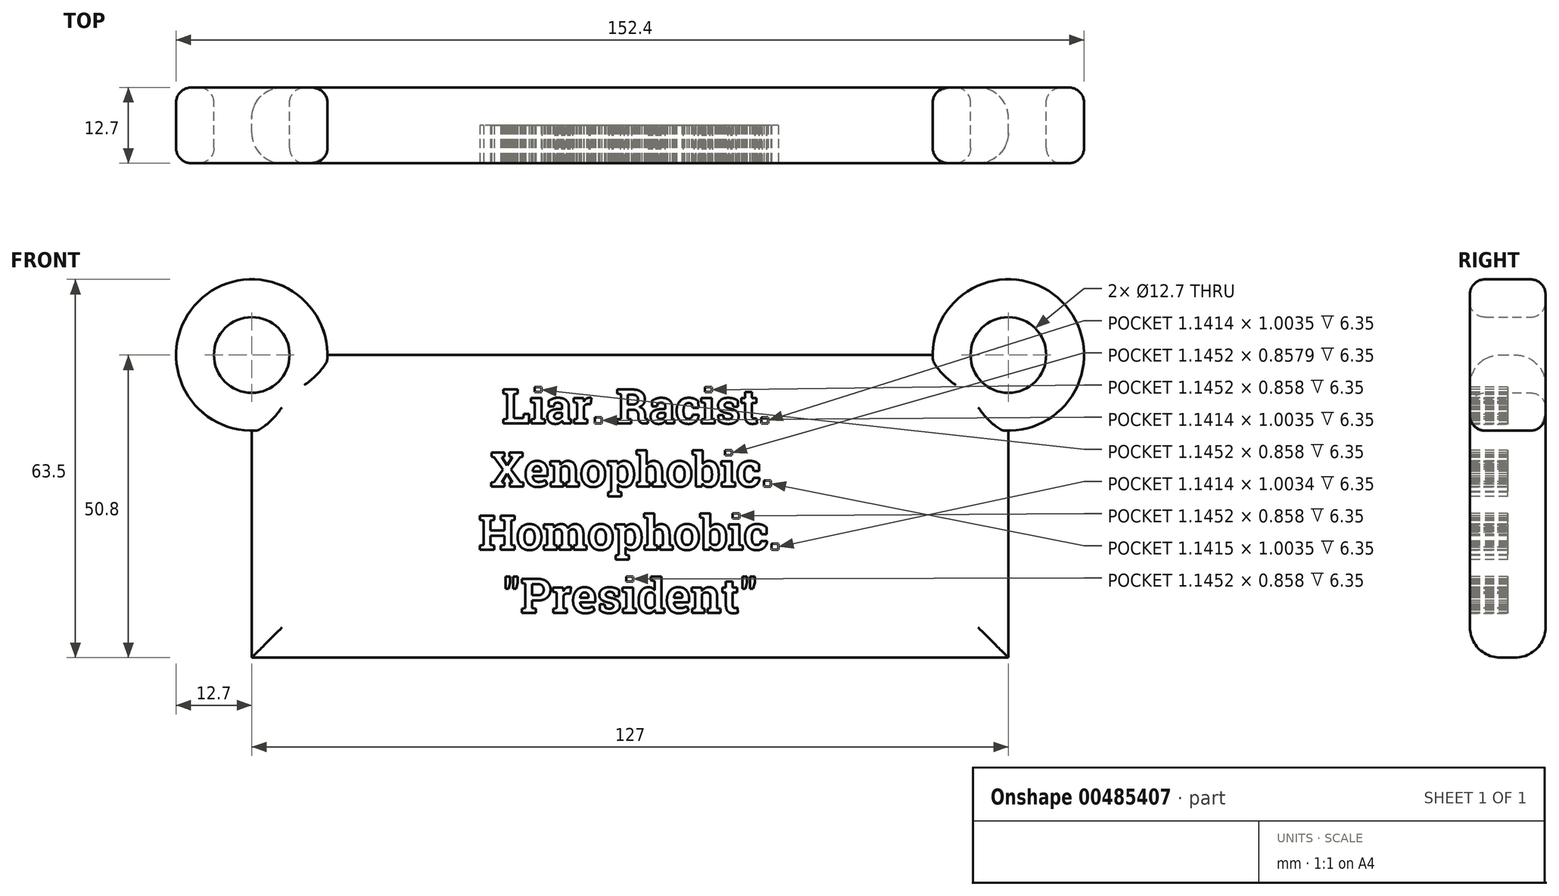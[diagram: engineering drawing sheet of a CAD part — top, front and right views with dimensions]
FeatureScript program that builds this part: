
annotation { "Feature Type Name" : "Feature", "Feature Type Description" : "" }
export const myFeature = defineFeature(function(context is Context, id is Id, definition is map)
    precondition{}
    {
        {
            var Q0;
            Q0=qCreatedBy(makeId("Front.planeOp"),FACE);
            var sketch = newSketch(context, id + "F0", { "sketchPlane" : qUnion([Q0])});
            skLineSegment(sketch, "E0.bottom", {"start": v(-127, 50.8) * mm, "end": v(0, 50.8) * mm});
            skLineSegment(sketch, "E0.top", {"start": v(-127, 0) * mm, "end": v(0, 0) * mm});
            skLineSegment(sketch, "E0.left", {"start": v(-127, 50.8) * mm, "end": v(-127, 0) * mm});
            skLineSegment(sketch, "E0.right", {"start": v(0, 50.8) * mm, "end": v(0, 0) * mm});
            skCircle(sketch, "E1", {"center": v(-127, 50.8) * mm, "radius": 6.35 * mm});
            skCircle(sketch, "E2", {"center": v(0, 50.8) * mm, "radius": 12.7 * mm});
            skCircle(sketch, "E3", {"center": v(0, 50.8) * mm, "radius": 6.35 * mm});
            skCircle(sketch, "E4", {"center": v(-127, 50.8) * mm, "radius": 12.7 * mm});
            skSolve(sketch);
        }
        {
            var Q0;
            Q0=qSketchRegion(id+"F0",true);
            extrude(context, id + "F1", {"entities" : qUnion([Q0]), "depth" : 12.7 * mm});
        }
        {
            var Q0;
            Q0=makeQuery(id+"F1.opExtrude","CAP_FACE",FACE,{"disambiguationData":[OSD([sQuery(id+"F0.wireOp",EDGE,"E0.bottom"),sQuery(id+"F0.wireOp",EDGE,"E0.top"),sQuery(id+"F0.wireOp",EDGE,"E0.left"),sQuery(id+"F0.wireOp",EDGE,"E0.right"),sQuery(id+"F0.wireOp",EDGE,"E1"),sQuery(id+"F0.wireOp",EDGE,"E2"),sQuery(id+"F0.wireOp",EDGE,"E3"),sQuery(id+"F0.wireOp",EDGE,"E4")])],"isStart":false});
            var sketch = newSketch(context, id + "F2", { "sketchPlane" : qUnion([Q0])});
            skText(sketch, "E5", { "text": "  Liar. Racist.\n Xenophobic.\nHomophobic.\n  \"President\"", "fontName": "RobotoSlab-Bold.ttf"});
            const initialGuessF2  = {"E5": [-0.0889, 0.0393, 1, 0, 0.00578]};
            skSetInitialGuess(sketch, initialGuessF2);
            skSolve(sketch);
        }
        {
            var Q0;
            Q0=qSketchRegion(id+"F2",true);
            extrude(context, id + "F3", {"entities" : qUnion([Q0]), "operationType" : NewBodyOperationType.REMOVE, "oppositeDirection" : true, "depth" : 6.35 * mm});
        }
        {
            var Q0;
            Q0=makeQuery(id+"F1.opExtrude","CAP_EDGE",EDGE,{"disambiguationData":[OSD([sQuery(id+"F0.wireOp",EDGE,"E1")])],"isStart":false});
            var Q1;
            Q1=makeQuery(id+"F1.opExtrude","CAP_EDGE",EDGE,{"disambiguationData":[OSD([sQuery(id+"F0.wireOp",EDGE,"E3")])],"isStart":false});
            var Q2;
            Q2=makeQuery(id+"F1.opExtrude","CAP_EDGE",EDGE,{"disambiguationData":[OSD([sQuery(id+"F0.wireOp",EDGE,"E1")])],"isStart":true});
            var Q3;
            Q3=makeQuery(id+"F1.opExtrude","CAP_EDGE",EDGE,{"disambiguationData":[OSD([sQuery(id+"F0.wireOp",EDGE,"E3")])],"isStart":true});
            var Q4;
            Q4=makeQuery(id+"F1.opExtrude","CAP_EDGE",EDGE,{"disambiguationData":[OSD([sQuery(id+"F0.wireOp",EDGE,"E4")])],"isStart":false});
            var Q5;
            Q5=makeQuery(id+"F1.opExtrude","CAP_EDGE",EDGE,{"disambiguationData":[OSD([sQuery(id+"F0.wireOp",EDGE,"E4")])],"isStart":true});
            var Q6;
            Q6=makeQuery(id+"F1.opExtrude","CAP_EDGE",EDGE,{"disambiguationData":[OSD([sQuery(id+"F0.wireOp",EDGE,"E2")])],"isStart":true});
            var Q7;
            Q7=makeQuery(id+"F1.opExtrude","CAP_EDGE",EDGE,{"disambiguationData":[OSD([sQuery(id+"F0.wireOp",EDGE,"E2")])],"isStart":false});
            fillet(context, id + "F4", {"entities" : qUnion([Q0, Q1, Q2, Q3, Q4, Q5, Q6, Q7]), "radius" : 2.54 * mm, "tangentPropagation" : true, "allowEdgeOverflow" : false});
        }
        {
            var Q0;
            Q0=makeQuery(id+"F1.opExtrude","CAP_EDGE",EDGE,{"disambiguationData":[OSD([sQuery(id+"F0.wireOp",EDGE,"E0.bottom")])],"isStart":false});
            var Q1;
            Q1=makeQuery(id+"F1.opExtrude","CAP_EDGE",EDGE,{"disambiguationData":[OSD([sQuery(id+"F0.wireOp",EDGE,"E0.bottom")])],"isStart":true});
            var Q2;
            Q2=makeQuery(id+"F1.opExtrude","CAP_EDGE",EDGE,{"disambiguationData":[OSD([sQuery(id+"F0.wireOp",EDGE,"E0.right")])],"isStart":false});
            var Q3;
            Q3=makeQuery(id+"F1.opExtrude","CAP_EDGE",EDGE,{"disambiguationData":[OSD([sQuery(id+"F0.wireOp",EDGE,"E0.right")])],"isStart":true});
            var Q4;
            Q4=makeQuery(id+"F1.opExtrude","CAP_EDGE",EDGE,{"disambiguationData":[OSD([sQuery(id+"F0.wireOp",EDGE,"E0.top")])],"isStart":false});
            var Q5;
            Q5=makeQuery(id+"F1.opExtrude","CAP_EDGE",EDGE,{"disambiguationData":[OSD([sQuery(id+"F0.wireOp",EDGE,"E0.left")])],"isStart":false});
            var Q6;
            Q6=makeQuery(id+"F1.opExtrude","CAP_EDGE",EDGE,{"disambiguationData":[OSD([sQuery(id+"F0.wireOp",EDGE,"E0.top")])],"isStart":true});
            var Q7;
            Q7=makeQuery(id+"F1.opExtrude","CAP_EDGE",EDGE,{"disambiguationData":[OSD([sQuery(id+"F0.wireOp",EDGE,"E0.left")])],"isStart":true});
            fillet(context, id + "F5", {"entities" : qUnion([Q0, Q1, Q2, Q3, Q4, Q5, Q6, Q7]), "radius" : 5.08 * mm, "tangentPropagation" : true, "allowEdgeOverflow" : false});
        }
    });
